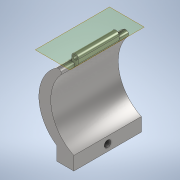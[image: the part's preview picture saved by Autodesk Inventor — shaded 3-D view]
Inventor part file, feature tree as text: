
AUTODESK INVENTOR PART (.ipt)
format: ipt  version: 2021 (Build 250183000, 183)  size: 179,712 bytes
history: native  units: in
note: dims shown in document units (in); Inventor stores cm internally (conversion verified against a paired STEP export)
features: sketch x6, extrude x5, fillet x3, plane x1, hole x1
ambient origin geometry x8: Origin, YZ Plane, XZ Plane, XY Plane, X Axis, Y Axis, Z Axis, Center Point
bodies: Solid1 (feature_tree)
feature tree (16):
  extrude  "Extrusion1"  Depth=3.937in TaperAngle=0.0deg
  extrude  "Extrusion2"  Depth=0.1969in
  plane  "Work Plane1"
  extrude  "Extrusion3"  Depth=3.937in TaperAngle=0.0deg
  extrude  "Extrusion4"  Depth=0.7874in
  extrude  "Extrusion5"  Depth=0.4724in
  hole  "Hole1"  [1 undecoded]
  fillet  "Fillet1"  Radius=0.3937in
  fillet  "Fillet2"  Radius=0.1181in
  fillet  "Fillet3"  Radius=0.9843in
  sketch  "Sketch1"  dims[d1=3.937in d2=2.3622in d3=0.7874in d5=0.4724in d6=3.937in d7=1.1811in d8=0.3937in d9=3.937in d10=0.0in]
  sketch  "Sketch2"  dims[d11=0.2756in d12=0.1969in]
  sketch  "Sketch3"  dims[d13=0.3937in d14=3.937in d15=0.0in]
  sketch  "Sketch4"  dims[d17=0.4724in d18=0.0in d19=0.7874in]
  sketch  "Sketch5"  dims[d20=0.4724in d21=0.0in d22=0.2756in]
  sketch  "Sketch6"  dims[d23=2.3622in d24=0.0in d25=0.3937in d26=0.3937in d27=0.3937in d28=0.2362in d29=0.1575in d30=0.0787in d31=90.0deg d32=0.315in d33=0.8108in d34=0.1181in d35=0.9843in d37=2.3622in d38=0.7874in d39=0.1575in d40=0.1181in d41=0.7874in d42=0.0197in d43=0.0344in d44=0.0197in d45=0.0344in]
note: 1 required parameter value undecoded (feature->parameter linkage not recoverable at this tier; creation-order binding heuristic only, values carry confidence <= 0.55)
